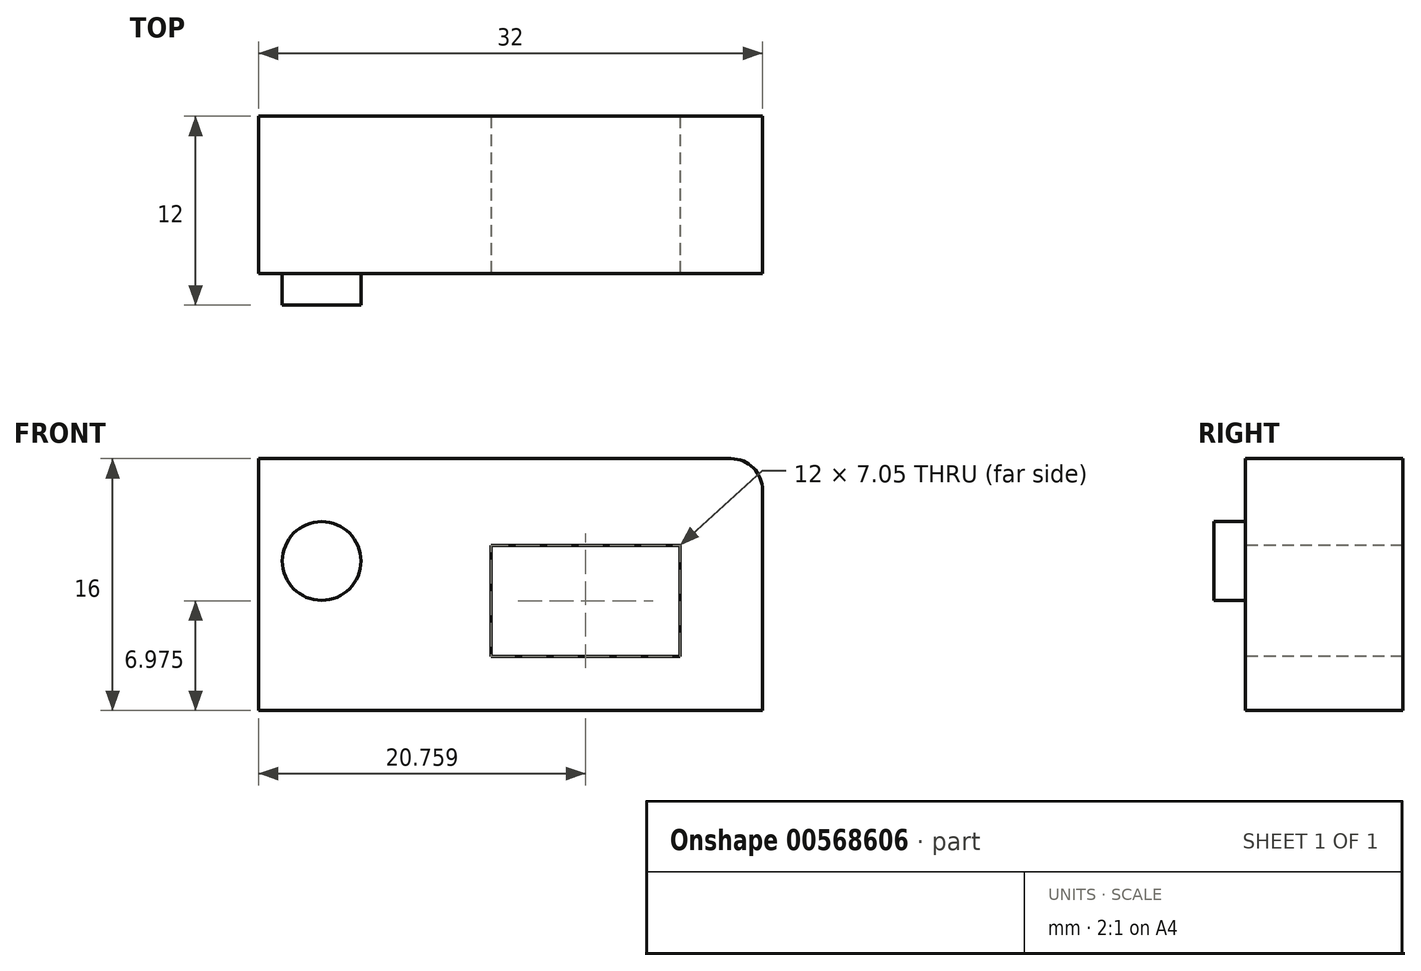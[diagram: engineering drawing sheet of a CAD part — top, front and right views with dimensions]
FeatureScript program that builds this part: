
annotation { "Feature Type Name" : "Feature", "Feature Type Description" : "" }
export const myFeature = defineFeature(function(context is Context, id is Id, definition is map)
    precondition{}
    {
        {
            var Q0;
            Q0=qCreatedBy(makeId("Front.planeOp"),FACE);
            var sketch = newSketch(context, id + "F0", { "sketchPlane" : qUnion([Q0])});
            skLineSegment(sketch, "E0.bottom", {"start": v(0, 0) * mm, "end": v(-32, 0) * mm});
            skLineSegment(sketch, "E0.top", {"start": v(0, 16) * mm, "end": v(-32, 16) * mm});
            skLineSegment(sketch, "E0.left", {"start": v(0, 0) * mm, "end": v(0, 16) * mm});
            skLineSegment(sketch, "E0.right", {"start": v(-32, 0) * mm, "end": v(-32, 16) * mm});
            skSolve(sketch);
        }
        {
            var Q0;
            Q0 = qSketchRegion(id + "F0", true);
            extrude(context, id + "F1", {"entities" : qUnion([Q0]), "depth" : 10 * mm, "offsetDistance" : 25 * mm});
        }
        {
            var Q0;
            Q0=makeQuery(id+"F1.opExtrude","CAP_FACE",FACE,{"disambiguationData":[OSD([sQuery(id+"F0.wireOp",EDGE,"E0.bottom"),sQuery(id+"F0.wireOp",EDGE,"E0.top"),sQuery(id+"F0.wireOp",EDGE,"E0.left"),sQuery(id+"F0.wireOp",EDGE,"E0.right")])],"isStart":false});
            var sketch = newSketch(context, id + "F2", { "sketchPlane" : qUnion([Q0])});
            skCircle(sketch, "E1", {"center": v(-28, 9.5) * mm, "radius": 2.5 * mm});
            skSolve(sketch);
        }
        {
            var Q0;
            Q0 = qSketchRegion(id + "F2", true);
            extrude(context, id + "F3", {"entities" : qUnion([Q0]), "operationType" : NewBodyOperationType.ADD, "depth" : 2 * mm, "offsetDistance" : 25 * mm});
        }
        {
            var Q0;
            Q0=makeQuery(id+"F1.opExtrude","SWEPT_EDGE",EDGE,{"disambiguationData":[OSD([sQuery(id+"F0.wireOp",EDGE,"E0.top"),sQuery(id+"F0.wireOp",EDGE,"E0.left")])]});
            fillet(context, id + "F4", {"entities" : qUnion([Q0]), "radius" : 2 * mm, "tangentPropagation" : true, "allowEdgeOverflow" : false});
        }
        {
            var Q0;
            Q0=makeQuery(id+"F1.opExtrude","CAP_FACE",FACE,{"disambiguationData":[OSD([sQuery(id+"F0.wireOp",EDGE,"E0.bottom"),sQuery(id+"F0.wireOp",EDGE,"E0.top"),sQuery(id+"F0.wireOp",EDGE,"E0.left"),sQuery(id+"F0.wireOp",EDGE,"E0.right")])],"isStart":false});
            var sketch = newSketch(context, id + "F5", { "sketchPlane" : qUnion([Q0])});
            skLineSegment(sketch, "E2.bottom", {"start": v(-17.24, 10.5) * mm, "end": v(-5.24, 10.5) * mm});
            skLineSegment(sketch, "E2.top", {"start": v(-17.24, 3.45) * mm, "end": v(-5.24, 3.45) * mm});
            skLineSegment(sketch, "E2.left", {"start": v(-17.24, 10.5) * mm, "end": v(-17.24, 3.45) * mm});
            skLineSegment(sketch, "E2.right", {"start": v(-5.24, 10.5) * mm, "end": v(-5.24, 3.45) * mm});
            skSolve(sketch);
        }
        {
            var Q0;
            Q0 = qSketchRegion(id + "F5", true);
            var Q1;
            Q1=makeQuery(id+"F1.opExtrude","CAP_FACE",FACE,{"disambiguationData":[OSD([sQuery(id+"F0.wireOp",EDGE,"E0.bottom"),sQuery(id+"F0.wireOp",EDGE,"E0.top"),sQuery(id+"F0.wireOp",EDGE,"E0.left"),sQuery(id+"F0.wireOp",EDGE,"E0.right")])],"isStart":true});
            extrude(context, id + "F6", {"entities" : qUnion([Q0]), "operationType" : NewBodyOperationType.REMOVE, "endBound" : BoundingType.UP_TO_SURFACE, "oppositeDirection" : true, "depth" : 25 * mm, "endBoundEntityFace" : qUnion([Q1]), "offsetDistance" : 25 * mm});
        }
    });
